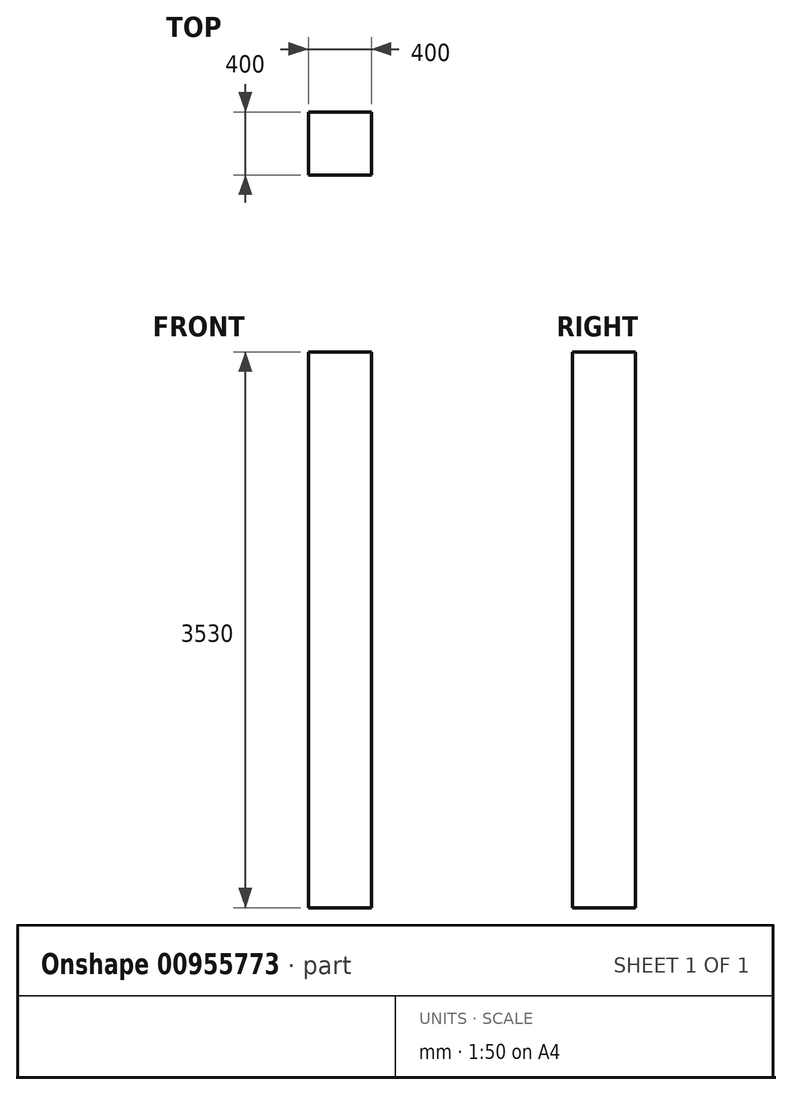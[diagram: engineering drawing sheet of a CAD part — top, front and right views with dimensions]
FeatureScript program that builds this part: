
annotation { "Feature Type Name" : "Feature", "Feature Type Description" : "" }
export const myFeature = defineFeature(function(context is Context, id is Id, definition is map)
    precondition{}
    {
        {
            var Q0;
            Q0=qCreatedBy(makeId("Top.planeOp"),FACE);
            var sketch = newSketch(context, id + "F0", { "sketchPlane" : qUnion([Q0])});
            skLineSegment(sketch, "E0.bottom", {"start": v(-318.96, 340.36) * mm, "end": v(81.04, 340.36) * mm});
            skLineSegment(sketch, "E0.top", {"start": v(-318.96, -59.64) * mm, "end": v(81.04, -59.64) * mm});
            skLineSegment(sketch, "E0.left", {"start": v(-318.96, 340.36) * mm, "end": v(-318.96, -59.64) * mm});
            skLineSegment(sketch, "E0.right", {"start": v(81.04, 340.36) * mm, "end": v(81.04, -59.64) * mm});
            skSolve(sketch);
        }
        {
            var Q0;
            Q0=makeQuery(id+"F0.imprint","IMPRINT",FACE,{"disambiguationData":[TD([[makeQuery(id+"F0.imprint","IMPRINT",EDGE,{"derivedFrom":sQuery(id+"F0.wireOp",EDGE,"E0.bottom")}),-1.0]])]});
            extrude(context, id + "F1", {"entities" : qUnion([Q0]), "depth" : 3530 * mm, "offsetDistance" : 25.4 * mm});
        }
    });
